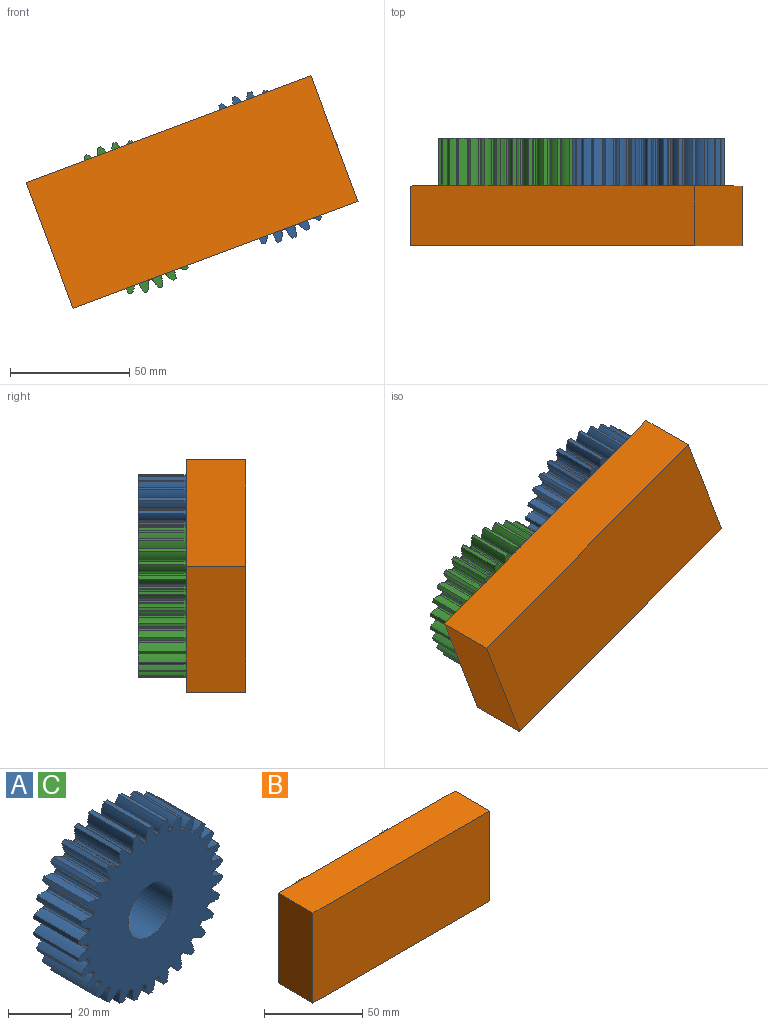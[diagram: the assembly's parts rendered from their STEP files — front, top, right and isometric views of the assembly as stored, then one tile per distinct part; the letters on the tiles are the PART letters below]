
ASSEMBLY  parts=3 mates=2
PART A: 183 faces, bbox 63.8x20x64 mm
  f0: extruded ~20x3.75mm, area 81.8mm2, adj f120,f121,f122,f123
  f1: cylinder r=27.5mm len=20mm, axis (0,1,0), area 14.4mm2, adj f121,f122,f123,f124
  f2: extruded ~20x3.75mm, area 81.8mm2, adj f3,f121,f122,f124
  f3: cylinder r=32mm len=20mm, axis (0,1,0), area 29.4mm2, adj f2,f4,f121,f122
  f4: extruded ~20x3.99mm, area 81.8mm2, adj f3,f121,f122,f125
  f5: cylinder r=27.5mm len=20mm, axis (0,1,0), area 14.4mm2, adj f121,f122,f125,f126
  f6: extruded ~20x3.34mm, area 81.8mm2, adj f7,f121,f122,f126
  f7: cylinder r=32mm len=20mm, axis (0,1,0), area 29.4mm2, adj f6,f8,f121,f122
  f8: extruded ~20x4.06mm, area 81.8mm2, adj f7,f121,f122,f127
  f9: cylinder r=27.5mm len=20mm, axis (0,1,0), area 14.4mm2, adj f121,f122,f127,f128
  f10: extruded ~20x2.95mm, area 81.8mm2, adj f11,f121,f122,f128
  f11: cylinder r=32mm len=20mm, axis (0,1,0), area 29.4mm2, adj f10,f12,f121,f122
  f12: extruded ~20x3.95mm, area 81.8mm2, adj f11,f121,f122,f129
  f13: cylinder r=27.5mm len=20mm, axis (0,1,0), area 14.4mm2, adj f121,f122,f129,f130
  f14: extruded ~20x3.46mm, area 81.8mm2, adj f15,f121,f122,f130
  f15: cylinder r=32mm len=20mm, axis (0,1,0), area 29.4mm2, adj f14,f16,f121,f122
  f16: extruded ~20x3.67mm, area 81.8mm2, adj f15,f121,f122,f131
  f17: cylinder r=27.5mm len=20mm, axis (0,1,0), area 14.4mm2, adj f121,f122,f131,f132
  f18: extruded ~20x3.83mm, area 81.8mm2, adj f19,f121,f122,f132
  f19: cylinder r=32mm len=20mm, axis (0,1,0), area 29.4mm2, adj f18,f20,f121,f122
  f20: extruded ~20x3.22mm, area 81.8mm2, adj f19,f121,f122,f133
  f21: cylinder r=27.5mm len=20mm, axis (0,1,0), area 14.4mm2, adj f121,f122,f133,f134
  f22: extruded ~20x4.02mm, area 81.8mm2, adj f23,f121,f122,f134
  f23: cylinder r=32mm len=20mm, axis (0,1,0), area 29.4mm2, adj f22,f24,f121,f122
  f24: extruded ~20x3.08mm, area 81.8mm2, adj f23,f121,f122,f135
  f25: cylinder r=27.5mm len=20mm, axis (0,1,0), area 14.4mm2, adj f121,f122,f135,f136
  f26: extruded ~20x4.04mm, area 81.8mm2, adj f27,f121,f122,f136
  f27: cylinder r=32mm len=20mm, axis (0,1,0), area 29.4mm2, adj f26,f28,f121,f122
  f28: extruded ~20x3.56mm, area 81.8mm2, adj f27,f121,f122,f137
  f29: cylinder r=27.5mm len=20mm, axis (0,1,0), area 14.4mm2, adj f121,f122,f137,f138
  f30: extruded ~20x3.89mm, area 81.8mm2, adj f31,f121,f122,f138
  f31: cylinder r=32mm len=20mm, axis (0,1,0), area 29.4mm2, adj f30,f32,f121,f122
  f32: extruded ~20x3.89mm, area 81.8mm2, adj f31,f121,f122,f139
  f33: cylinder r=27.5mm len=20mm, axis (0,1,0), area 14.4mm2, adj f121,f122,f139,f140
  f34: extruded ~20x3.56mm, area 81.8mm2, adj f35,f121,f122,f140
  f35: cylinder r=32mm len=20mm, axis (0,1,0), area 29.4mm2, adj f34,f36,f121,f122
  f36: extruded ~20x4.04mm, area 81.8mm2, adj f35,f121,f122,f141
  f37: cylinder r=27.5mm len=20mm, axis (0,1,0), area 14.4mm2, adj f121,f122,f141,f142
  f38: extruded ~20x3.08mm, area 81.8mm2, adj f39,f121,f122,f142
  f39: cylinder r=32mm len=20mm, axis (0,1,0), area 29.4mm2, adj f38,f40,f121,f122
  f40: extruded ~20x4.02mm, area 81.8mm2, adj f39,f121,f122,f143
  f41: cylinder r=27.5mm len=20mm, axis (0,1,0), area 14.4mm2, adj f121,f122,f143,f144
  f42: extruded ~20x3.22mm, area 81.8mm2, adj f43,f121,f122,f144
  f43: cylinder r=32mm len=20mm, axis (0,1,0), area 29.4mm2, adj f42,f44,f121,f122
  f44: extruded ~20x3.83mm, area 81.8mm2, adj f43,f121,f122,f145
  f45: cylinder r=27.5mm len=20mm, axis (0,1,0), area 14.4mm2, adj f121,f122,f145,f146
  f46: extruded ~20x3.67mm, area 81.8mm2, adj f47,f121,f122,f146
  f47: cylinder r=32mm len=20mm, axis (0,1,0), area 29.4mm2, adj f46,f48,f121,f122
  f48: extruded ~20x3.46mm, area 81.8mm2, adj f47,f121,f122,f147
  f49: cylinder r=27.5mm len=20mm, axis (0,1,0), area 14.4mm2, adj f121,f122,f147,f148
  f50: extruded ~20x3.95mm, area 81.8mm2, adj f51,f121,f122,f148
  f51: cylinder r=32mm len=20mm, axis (0,1,0), area 29.4mm2, adj f50,f52,f121,f122
  f52: extruded ~20x2.95mm, area 81.8mm2, adj f51,f121,f122,f149
  f53: cylinder r=27.5mm len=20mm, axis (0,1,0), area 14.4mm2, adj f121,f122,f149,f150
  f54: extruded ~20x4.06mm, area 81.8mm2, adj f55,f121,f122,f150
  f55: cylinder r=32mm len=20mm, axis (0,1,0), area 29.4mm2, adj f54,f56,f121,f122
  f56: extruded ~20x3.34mm, area 81.8mm2, adj f55,f121,f122,f151
  f57: cylinder r=27.5mm len=20mm, axis (0,1,0), area 14.4mm2, adj f121,f122,f151,f152
  f58: extruded ~20x3.99mm, area 81.8mm2, adj f59,f121,f122,f152
  f59: cylinder r=32mm len=20mm, axis (0,1,0), area 29.4mm2, adj f58,f60,f121,f122
  f60: extruded ~20x3.75mm, area 81.8mm2, adj f59,f121,f122,f153
  f61: cylinder r=27.5mm len=20mm, axis (0,1,0), area 14.4mm2, adj f121,f122,f153,f154
  f62: extruded ~20x3.75mm, area 81.8mm2, adj f63,f121,f122,f154
  f63: cylinder r=32mm len=20mm, axis (0,1,0), area 29.4mm2, adj f62,f64,f121,f122
  f64: extruded ~20x3.99mm, area 81.8mm2, adj f63,f121,f122,f155
  f65: cylinder r=27.5mm len=20mm, axis (0,1,0), area 14.4mm2, adj f121,f122,f155,f156
  f66: extruded ~20x3.34mm, area 81.8mm2, adj f67,f121,f122,f156
  f67: cylinder r=32mm len=20mm, axis (0,1,0), area 29.4mm2, adj f66,f68,f121,f122
  f68: extruded ~20x4.06mm, area 81.8mm2, adj f67,f121,f122,f157
  f69: cylinder r=27.5mm len=20mm, axis (0,1,0), area 14.4mm2, adj f121,f122,f157,f158
  f70: extruded ~20x2.95mm, area 81.8mm2, adj f71,f121,f122,f158
  f71: cylinder r=32mm len=20mm, axis (0,1,0), area 29.4mm2, adj f70,f72,f121,f122
  f72: extruded ~20x3.95mm, area 81.8mm2, adj f71,f121,f122,f159
  f73: cylinder r=27.5mm len=20mm, axis (0,1,0), area 14.4mm2, adj f121,f122,f159,f160
  f74: extruded ~20x3.46mm, area 81.8mm2, adj f75,f121,f122,f160
  f75: cylinder r=32mm len=20mm, axis (0,1,0), area 29.4mm2, adj f74,f76,f121,f122
  f76: extruded ~20x3.67mm, area 81.8mm2, adj f75,f121,f122,f161
  f77: cylinder r=27.5mm len=20mm, axis (0,1,0), area 14.4mm2, adj f121,f122,f161,f162
  f78: extruded ~20x3.83mm, area 81.8mm2, adj f79,f121,f122,f162
  f79: cylinder r=32mm len=20mm, axis (0,1,0), area 29.4mm2, adj f78,f80,f121,f122
  f80: extruded ~20x3.22mm, area 81.8mm2, adj f79,f121,f122,f163
  f81: cylinder r=27.5mm len=20mm, axis (0,1,0), area 14.4mm2, adj f121,f122,f163,f164
  f82: extruded ~20x4.02mm, area 81.8mm2, adj f83,f121,f122,f164
  f83: cylinder r=32mm len=20mm, axis (0,1,0), area 29.4mm2, adj f82,f84,f121,f122
  f84: extruded ~20x3.08mm, area 81.8mm2, adj f83,f121,f122,f165
  f85: cylinder r=27.5mm len=20mm, axis (0,1,0), area 14.4mm2, adj f121,f122,f165,f166
  f86: extruded ~20x4.04mm, area 81.8mm2, adj f87,f121,f122,f166
  f87: cylinder r=32mm len=20mm, axis (0,1,0), area 29.4mm2, adj f86,f88,f121,f122
  f88: extruded ~20x3.56mm, area 81.8mm2, adj f87,f121,f122,f167
  f89: cylinder r=27.5mm len=20mm, axis (0,1,0), area 14.4mm2, adj f121,f122,f167,f168
  f90: extruded ~20x3.89mm, area 81.8mm2, adj f91,f121,f122,f168
  f91: cylinder r=32mm len=20mm, axis (0,1,0), area 29.4mm2, adj f90,f92,f121,f122
  f92: extruded ~20x3.89mm, area 81.8mm2, adj f91,f121,f122,f169
  f93: cylinder r=27.5mm len=20mm, axis (0,1,0), area 14.4mm2, adj f121,f122,f169,f170
  f94: extruded ~20x3.56mm, area 81.8mm2, adj f95,f121,f122,f170
  f95: cylinder r=32mm len=20mm, axis (0,1,0), area 29.4mm2, adj f94,f96,f121,f122
  f96: extruded ~20x4.04mm, area 81.8mm2, adj f95,f121,f122,f171
  f97: cylinder r=27.5mm len=20mm, axis (0,1,0), area 14.4mm2, adj f121,f122,f171,f172
  f98: extruded ~20x3.08mm, area 81.8mm2, adj f99,f121,f122,f172
  f99: cylinder r=32mm len=20mm, axis (0,1,0), area 29.4mm2, adj f98,f100,f121,f122
  f100: extruded ~20x4.02mm, area 81.8mm2, adj f99,f121,f122,f173
  f101: cylinder r=27.5mm len=20mm, axis (0,1,0), area 14.4mm2, adj f121,f122,f173,f174
  f102: extruded ~20x3.22mm, area 81.8mm2, adj f103,f121,f122,f174
  f103: cylinder r=32mm len=20mm, axis (0,1,0), area 29.4mm2, adj f102,f104,f121,f122
  f104: extruded ~20x3.83mm, area 81.8mm2, adj f103,f121,f122,f175
  f105: cylinder r=27.5mm len=20mm, axis (0,1,0), area 14.4mm2, adj f121,f122,f175,f176
  f106: extruded ~20x3.67mm, area 81.8mm2, adj f107,f121,f122,f176
  f107: cylinder r=32mm len=20mm, axis (0,1,0), area 29.4mm2, adj f106,f108,f121,f122
  f108: extruded ~20x3.46mm, area 81.8mm2, adj f107,f121,f122,f177
  f109: cylinder r=27.5mm len=20mm, axis (0,1,0), area 14.4mm2, adj f121,f122,f177,f178
  f110: extruded ~20x3.95mm, area 81.8mm2, adj f111,f121,f122,f178
  f111: cylinder r=32mm len=20mm, axis (0,1,0), area 29.4mm2, adj f110,f112,f121,f122
  f112: extruded ~20x2.95mm, area 81.8mm2, adj f111,f121,f122,f179
  f113: cylinder r=27.5mm len=20mm, axis (0,1,0), area 14.4mm2, adj f121,f122,f179,f180
  f114: extruded ~20x4.06mm, area 81.8mm2, adj f115,f121,f122,f180
  f115: cylinder r=32mm len=20mm, axis (0,1,0), area 29.4mm2, adj f114,f116,f121,f122
  f116: extruded ~20x3.34mm, area 81.8mm2, adj f115,f121,f122,f181
  f117: cylinder r=27.5mm len=20mm, axis (0,1,0), area 14.4mm2, adj f121,f122,f181,f182
  f118: extruded ~20x3.99mm, area 81.8mm2, adj f120,f121,f122,f182
  f119: cylinder r=10mm len=20mm, axis (0,1,0), area 1256.6mm2, adj f121,f122
  f120: cylinder r=32mm len=20mm, axis (0,1,0), area 29.4mm2, adj f0,f118,f121,f122
  f121: plane 64x63.79mm, normal (0,-1,0), area 2480.9mm2, adj f0,f1,f2,f3,f4,f5,f6,f7
  f122: plane 64x63.79mm, normal (0,1,0), area 2480.9mm2, adj f0,f1,f2,f3,f4,f5,f6,f7
  f123: cylinder r=0.69mm len=20mm, axis (0,1,0), area 21mm2, adj f0,f1,f121,f122
  f124: cylinder r=0.69mm len=20mm, axis (0,1,0), area 21mm2, adj f1,f2,f121,f122
  f125: cylinder r=0.69mm len=20mm, axis (0,1,0), area 21mm2, adj f4,f5,f121,f122
  f126: cylinder r=0.69mm len=20mm, axis (0,1,0), area 21mm2, adj f5,f6,f121,f122
  f127: cylinder r=0.69mm len=20mm, axis (0,1,0), area 21mm2, adj f8,f9,f121,f122
  f128: cylinder r=0.69mm len=20mm, axis (0,1,0), area 21mm2, adj f9,f10,f121,f122
  f129: cylinder r=0.69mm len=20mm, axis (0,1,0), area 21mm2, adj f12,f13,f121,f122
  f130: cylinder r=0.69mm len=20mm, axis (0,1,0), area 21mm2, adj f13,f14,f121,f122
  f131: cylinder r=0.69mm len=20mm, axis (0,1,0), area 21mm2, adj f16,f17,f121,f122
  f132: cylinder r=0.69mm len=20mm, axis (0,1,0), area 21mm2, adj f17,f18,f121,f122
  f133: cylinder r=0.69mm len=20mm, axis (0,1,0), area 21mm2, adj f20,f21,f121,f122
  f134: cylinder r=0.69mm len=20mm, axis (0,1,0), area 21mm2, adj f21,f22,f121,f122
  f135: cylinder r=0.69mm len=20mm, axis (0,1,0), area 21mm2, adj f24,f25,f121,f122
  f136: cylinder r=0.69mm len=20mm, axis (0,1,0), area 21mm2, adj f25,f26,f121,f122
  f137: cylinder r=0.69mm len=20mm, axis (0,1,0), area 21mm2, adj f28,f29,f121,f122
  f138: cylinder r=0.69mm len=20mm, axis (0,1,0), area 21mm2, adj f29,f30,f121,f122
  f139: cylinder r=0.69mm len=20mm, axis (0,1,0), area 21mm2, adj f32,f33,f121,f122
  f140: cylinder r=0.69mm len=20mm, axis (0,1,0), area 21mm2, adj f33,f34,f121,f122
  f141: cylinder r=0.69mm len=20mm, axis (0,1,0), area 21mm2, adj f36,f37,f121,f122
  f142: cylinder r=0.69mm len=20mm, axis (0,1,0), area 21mm2, adj f37,f38,f121,f122
  f143: cylinder r=0.69mm len=20mm, axis (0,1,0), area 21mm2, adj f40,f41,f121,f122
  f144: cylinder r=0.69mm len=20mm, axis (0,1,0), area 21mm2, adj f41,f42,f121,f122
  f145: cylinder r=0.69mm len=20mm, axis (0,1,0), area 21mm2, adj f44,f45,f121,f122
  f146: cylinder r=0.69mm len=20mm, axis (0,1,0), area 21mm2, adj f45,f46,f121,f122
  f147: cylinder r=0.69mm len=20mm, axis (0,1,0), area 21mm2, adj f48,f49,f121,f122
  f148: cylinder r=0.69mm len=20mm, axis (0,1,0), area 21mm2, adj f49,f50,f121,f122
  f149: cylinder r=0.69mm len=20mm, axis (0,1,0), area 21mm2, adj f52,f53,f121,f122
  f150: cylinder r=0.69mm len=20mm, axis (0,1,0), area 21mm2, adj f53,f54,f121,f122
  f151: cylinder r=0.69mm len=20mm, axis (0,1,0), area 21mm2, adj f56,f57,f121,f122
  f152: cylinder r=0.69mm len=20mm, axis (0,1,0), area 21mm2, adj f57,f58,f121,f122
  f153: cylinder r=0.69mm len=20mm, axis (0,1,0), area 21mm2, adj f60,f61,f121,f122
  f154: cylinder r=0.69mm len=20mm, axis (0,1,0), area 21mm2, adj f61,f62,f121,f122
  f155: cylinder r=0.69mm len=20mm, axis (0,1,0), area 21mm2, adj f64,f65,f121,f122
  f156: cylinder r=0.69mm len=20mm, axis (0,1,0), area 21mm2, adj f65,f66,f121,f122
  f157: cylinder r=0.69mm len=20mm, axis (0,1,0), area 21mm2, adj f68,f69,f121,f122
  f158: cylinder r=0.69mm len=20mm, axis (0,1,0), area 21mm2, adj f69,f70,f121,f122
  f159: cylinder r=0.69mm len=20mm, axis (0,1,0), area 21mm2, adj f72,f73,f121,f122
  f160: cylinder r=0.69mm len=20mm, axis (0,1,0), area 21mm2, adj f73,f74,f121,f122
  f161: cylinder r=0.69mm len=20mm, axis (0,1,0), area 21mm2, adj f76,f77,f121,f122
  f162: cylinder r=0.69mm len=20mm, axis (0,1,0), area 21mm2, adj f77,f78,f121,f122
  f163: cylinder r=0.69mm len=20mm, axis (0,1,0), area 21mm2, adj f80,f81,f121,f122
  f164: cylinder r=0.69mm len=20mm, axis (0,1,0), area 21mm2, adj f81,f82,f121,f122
  f165: cylinder r=0.69mm len=20mm, axis (0,1,0), area 21mm2, adj f84,f85,f121,f122
  f166: cylinder r=0.69mm len=20mm, axis (0,1,0), area 21mm2, adj f85,f86,f121,f122
  f167: cylinder r=0.69mm len=20mm, axis (0,1,0), area 21mm2, adj f88,f89,f121,f122
  f168: cylinder r=0.69mm len=20mm, axis (0,1,0), area 21mm2, adj f89,f90,f121,f122
  f169: cylinder r=0.69mm len=20mm, axis (0,1,0), area 21mm2, adj f92,f93,f121,f122
  f170: cylinder r=0.69mm len=20mm, axis (0,1,0), area 21mm2, adj f93,f94,f121,f122
  f171: cylinder r=0.69mm len=20mm, axis (0,1,0), area 21mm2, adj f96,f97,f121,f122
  f172: cylinder r=0.69mm len=20mm, axis (0,1,0), area 21mm2, adj f97,f98,f121,f122
  f173: cylinder r=0.69mm len=20mm, axis (0,1,0), area 21mm2, adj f100,f101,f121,f122
  f174: cylinder r=0.69mm len=20mm, axis (0,1,0), area 21mm2, adj f101,f102,f121,f122
  f175: cylinder r=0.69mm len=20mm, axis (0,1,0), area 21mm2, adj f104,f105,f121,f122
  f176: cylinder r=0.69mm len=20mm, axis (0,1,0), area 21mm2, adj f105,f106,f121,f122
  f177: cylinder r=0.69mm len=20mm, axis (0,1,0), area 21mm2, adj f108,f109,f121,f122
  f178: cylinder r=0.69mm len=20mm, axis (0,1,0), area 21mm2, adj f109,f110,f121,f122
  f179: cylinder r=0.69mm len=20mm, axis (0,1,0), area 21mm2, adj f112,f113,f121,f122
  f180: cylinder r=0.69mm len=20mm, axis (0,1,0), area 21mm2, adj f113,f114,f121,f122
  f181: cylinder r=0.69mm len=20mm, axis (0,1,0), area 21mm2, adj f116,f117,f121,f122
  f182: cylinder r=0.69mm len=20mm, axis (0,1,0), area 21mm2, adj f117,f118,f121,f122
PART B: 10 faces, bbox 127.4x45x56.2 mm
  f0: plane 127.43x25mm, normal (0,0,1), area 3185.9mm2, adj f1,f3,f4,f5
  f1: plane 56.18x25mm, normal (-1,0,0), area 1404.5mm2, adj f0,f2,f4,f5
  f2: plane 127.43x25mm, normal (0,0,-1), area 3185.9mm2, adj f1,f3,f4,f5
  f3: plane 56.18x25mm, normal (1,0,0), area 1404.5mm2, adj f0,f2,f4,f5
  f4: plane 127.43x56.18mm, normal (0,-1,0), area 7159.4mm2, adj f0,f1,f2,f3
  f5: plane 127.43x56.18mm, normal (0,1,0), area 6531mm2, adj f0,f1,f2,f3,f6,f8
  f6: cylinder r=10mm len=20mm, axis (0,-1,0), area 1256.6mm2, adj f5,f7
  f7: plane 20x20mm, normal (0,1,0), area 314.2mm2, adj f6
  f8: cylinder r=10mm len=20mm, axis (0,-1,0), area 1256.6mm2, adj f5,f9
  f9: plane 20x20mm, normal (0,1,0), area 314.2mm2, adj f8
PART C: same geometry as A
PLACE A rot(axis=(0,-1,0),107.2deg) t=(87.22,12.04,-14.16)mm
PLACE B rot(axis=(0,-1,0),20.5deg) t=(7.08,-7.96,-73.22)mm fixed
PLACE C rot(axis=(0,-1,0),23.9deg) t=(31.03,12.04,-35.2)mm
MATE revolute A.f3 <-> B.f8  axis (0,1,0) through (87.22,12.04,-14.16)mm
MATE revolute C.f3 <-> B.f6  axis (0,1,0) through (31.03,12.04,-35.2)mm
